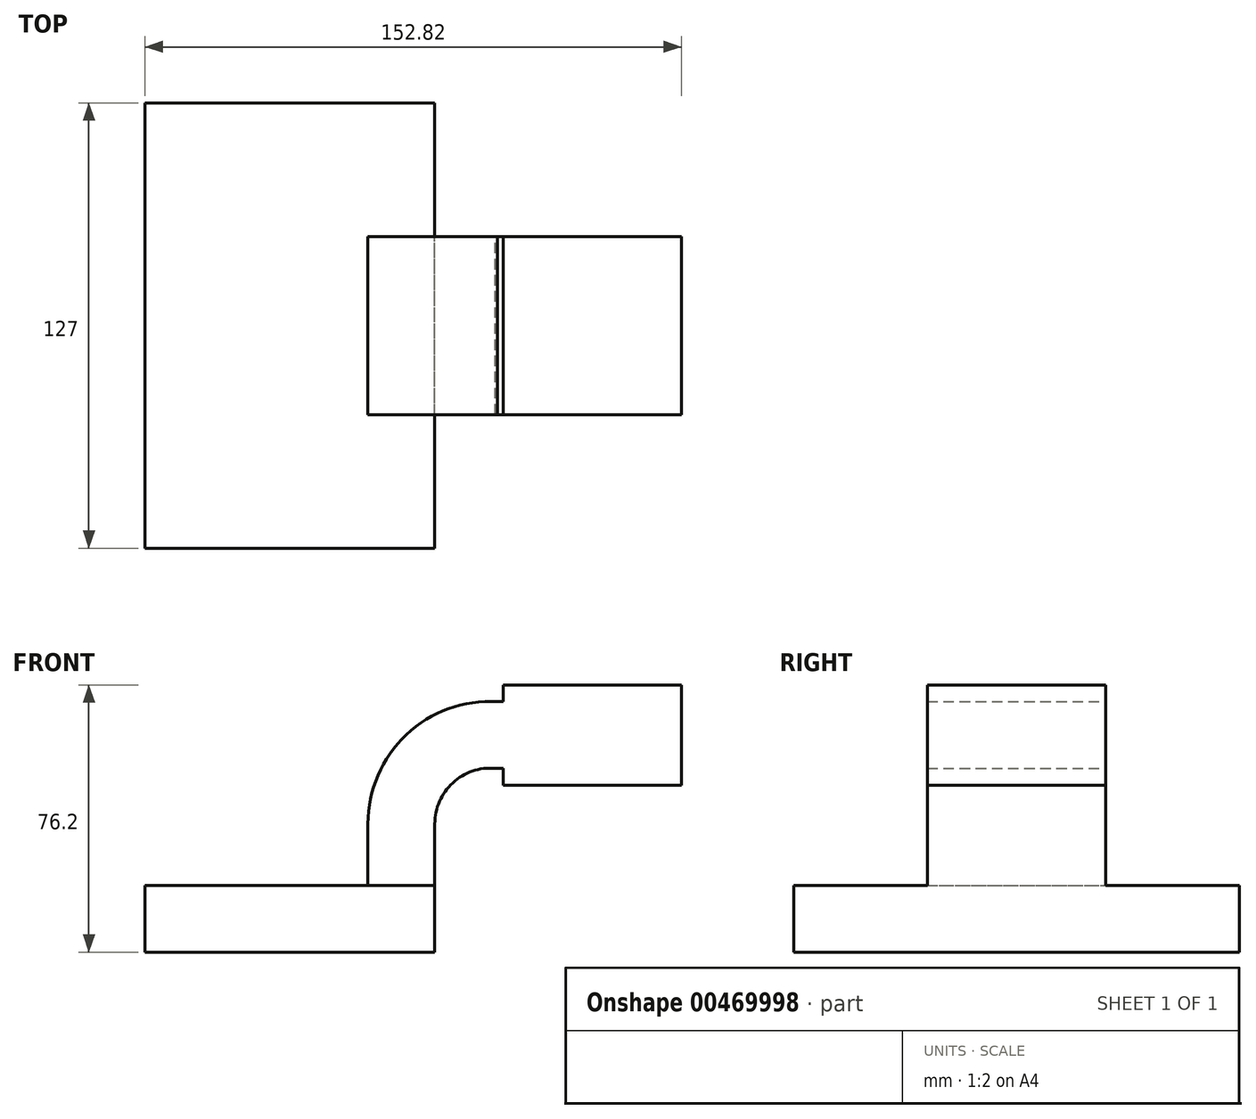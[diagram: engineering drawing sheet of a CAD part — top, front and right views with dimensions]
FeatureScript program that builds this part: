
annotation { "Feature Type Name" : "Feature", "Feature Type Description" : "" }
export const myFeature = defineFeature(function(context is Context, id is Id, definition is map)
    precondition{}
    {
        {
            var Q0;
            Q0=qCreatedBy(makeId("Front.planeOp"),FACE);
            var sketch = newSketch(context, id + "F0", { "sketchPlane" : qUnion([Q0])});
            skLineSegment(sketch, "E0.bottom", {"start": v(41.27, 9.53) * mm, "end": v(-41.28, 9.53) * mm});
            skLineSegment(sketch, "E0.top", {"start": v(41.28, -9.52) * mm, "end": v(-41.27, -9.52) * mm});
            skLineSegment(sketch, "E0.left", {"start": v(41.28, 9.53) * mm, "end": v(41.28, -9.52) * mm});
            skLineSegment(sketch, "E0.right", {"start": v(-41.28, 9.53) * mm, "end": v(-41.28, -9.52) * mm});
            skPoint(sketch, "E0.middle", {"position": v(0, 0) * mm});
            skLineSegment(sketch, "E1.bottom", {"start": v(60.74, 66.68) * mm, "end": v(111.54, 66.68) * mm});
            skLineSegment(sketch, "E1.top", {"start": v(60.74, 38.1) * mm, "end": v(111.54, 38.1) * mm});
            skLineSegment(sketch, "E1.left", {"start": v(60.74, 66.68) * mm, "end": v(60.74, 38.1) * mm});
            skLineSegment(sketch, "E1.right", {"start": v(111.54, 66.68) * mm, "end": v(111.54, 38.1) * mm});
            skPoint(sketch, "E1.middle", {"position": v(86.14, 52.39) * mm});
            skLineSegment(sketch, "E2", {"start": v(41.27, 9.53) * mm, "end": v(41.27, 27.06) * mm});
            skArc(sketch, "E3", {"start": v(41.27, 27.06) * mm, "mid": v(46.4, 38.74) * mm, "end": v(58.47, 42.88) * mm});
            skLineSegment(sketch, "E4", {"start": v(58.47, 42.88) * mm, "end": v(85.73, 42.88) * mm});
            skLineSegment(sketch, "E5.0", {"start": v(59.1, 61.93) * mm, "end": v(85.73, 61.93) * mm});
            skArc(sketch, "E5.1", {"start": v(22.22, 27.06) * mm, "mid": v(33.16, 52.43) * mm, "end": v(59.1, 61.93) * mm});
            skLineSegment(sketch, "E5.2", {"start": v(22.22, 9.53) * mm, "end": v(22.22, 27.06) * mm});
            skFitSpline(sketch, "E6", {"points": [v(-41.28, 9.52) * mm, v(59.1, 61.93) * mm], "startDerivative": vector(-1.42, 92.75) * mm, "endDerivative": vector(143.08, -10.9) * mm});
            skSolve(sketch);
        }
        {
            var Q0;
            Q0=makeQuery(id+"F0.imprint","IMPRINT",FACE,{"disambiguationData":[TD([[makeQuery(id+"F0.imprint","IMPRINT",EDGE,{"derivedFrom":sQuery(id+"F0.wireOp",EDGE,"E0.top")}),-1.0]])]});
            extrude(context, id + "F1", {"entities" : qUnion([Q0]), "endBound" : BoundingType.SYMMETRIC, "depth" : 127 * mm});
        }
        {
            var Q0;
            {var subQ1=sQuery(id+"F0.wireOp",EDGE,"E2");Q0=makeQuery(id+"F0.imprint","IMPRINT",FACE,{"disambiguationData":[TD([[makeQuery(id+"F0.imprint","IMPRINT",EDGE,{"derivedFrom":subQ1}),1.0]])]});}
            var Q1;
            {var subQ3=sQuery(id+"F0.wireOp",EDGE,"E1.bottom");Q1=makeQuery(id+"F0.imprint","IMPRINT",FACE,{"disambiguationData":[TD([[makeQuery(id+"F0.imprint","IMPRINT",EDGE,{"derivedFrom":subQ3}),-1.0]])]});}
            extrude(context, id + "F2", {"entities" : qUnion([Q0, Q1]), "operationType" : NewBodyOperationType.ADD, "endBound" : BoundingType.SYMMETRIC, "depth" : 50.8 * mm});
        }
        {
            var Q0;
            {var subQ3=sQuery(id+"F0.wireOp",EDGE,"E1.bottom");Q0=makeQuery(id+"F0.imprint","IMPRINT",FACE,{"disambiguationData":[TD([[makeQuery(id+"F0.imprint","IMPRINT",EDGE,{"derivedFrom":subQ3}),-1.0]])]});}
            var Q1;
            Q1=makeQuery(id+"F0.imprint","IMPRINT",FACE,{"disambiguationData":[TD([[makeQuery(id+"F0.imprint","IMPRINT",EDGE,{"derivedFrom":sQuery(id+"F0.wireOp",EDGE,"E0.top")}),-1.0]])]});
            var Q2;
            {var subQ1=sQuery(id+"F0.wireOp",EDGE,"E2");Q2=makeQuery(id+"F0.imprint","IMPRINT",FACE,{"disambiguationData":[TD([[makeQuery(id+"F0.imprint","IMPRINT",EDGE,{"derivedFrom":subQ1}),1.0]])]});}
            var Q3;
            Q3=makeQuery(id+"F0.imprint","IMPRINT",FACE,{"disambiguationData":[TD([[makeQuery(id+"F0.imprint","IMPRINT",EDGE,{"derivedFrom":sQuery(id+"F0.wireOp",EDGE,"E5.1")}),1.0]])]});
            extrude(context, id + "F3", {"entities" : qUnion([Q0, Q1, Q2, Q3]), "operationType" : NewBodyOperationType.ADD, "endBound" : BoundingType.SYMMETRIC, "depth" : 15.88 * mm});
        }
    });
